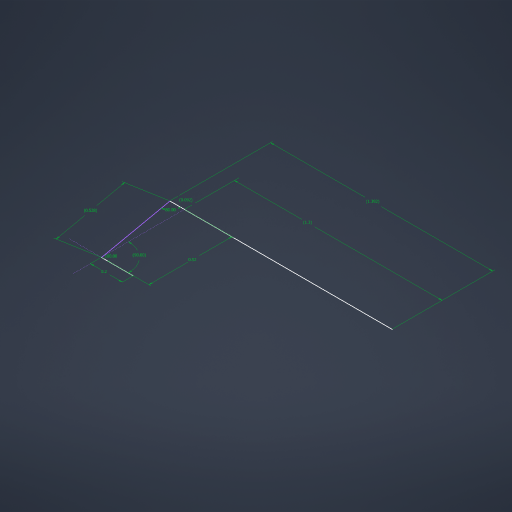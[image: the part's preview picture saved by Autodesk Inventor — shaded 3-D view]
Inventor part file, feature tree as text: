
AUTODESK INVENTOR PART (.ipt)
format: ipt  version: 2023 (Build 270158000, 158)  size: 171,520 bytes
history: native  units: mm
features: sketch x1
ambient origin geometry x8: Origin, YZ Plane, XZ Plane, XY Plane, X Axis, Y Axis, Z Axis, Center Point
feature tree (1):
  sketch  "Sketch1"  dims[d0=1.3mm d3=13.962634mm d4=0.2mm d7=17.453293mm d8=90.0deg d9=0.09169mm d10=0.52mm d11=0.528022mm d12=1.39169mm]
